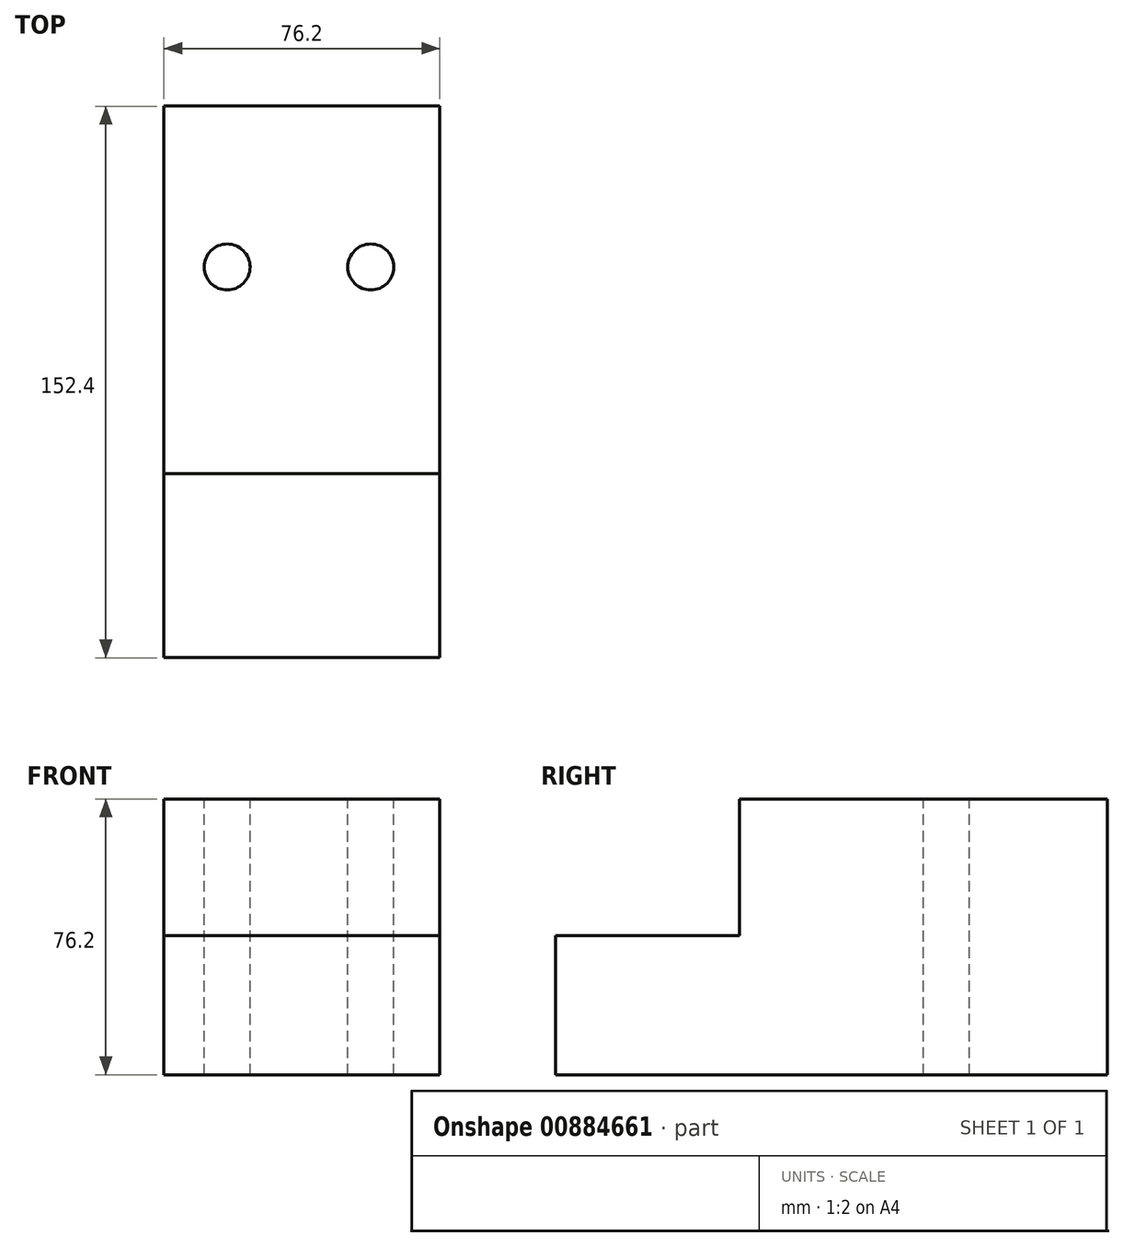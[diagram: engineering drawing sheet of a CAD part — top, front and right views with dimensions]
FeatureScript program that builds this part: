
annotation { "Feature Type Name" : "Feature", "Feature Type Description" : "" }
export const myFeature = defineFeature(function(context is Context, id is Id, definition is map)
    precondition{}
    {
        {
            var Q0;
            Q0=qCreatedBy(makeId("Top.planeOp"),FACE);
            var sketch = newSketch(context, id + "F0", { "sketchPlane" : qUnion([Q0])});
            skLineSegment(sketch, "E0.bottom", {"start": v(-21.8, 58.73) * mm, "end": v(54.4, 58.73) * mm});
            skLineSegment(sketch, "E0.top", {"start": v(-21.8, -93.67) * mm, "end": v(54.4, -93.67) * mm});
            skLineSegment(sketch, "E0.left", {"start": v(-21.8, 58.73) * mm, "end": v(-21.8, -93.67) * mm});
            skLineSegment(sketch, "E0.right", {"start": v(54.4, 58.73) * mm, "end": v(54.4, -93.67) * mm});
            skSolve(sketch);
        }
        {
            var Q0;
            Q0 = qSketchRegion(id + "F0", true);
            extrude(context, id + "F1", {"entities" : qUnion([Q0]), "depth" : 76.2 * mm, "offsetDistance" : 25.4 * mm});
        }
        {
            var Q0;
            Q0=makeQuery(id+"F1.opExtrude","CAP_FACE",FACE,{"disambiguationData":[OSD([sQuery(id+"F0.wireOp",EDGE,"E0.bottom"),sQuery(id+"F0.wireOp",EDGE,"E0.top"),sQuery(id+"F0.wireOp",EDGE,"E0.left"),sQuery(id+"F0.wireOp",EDGE,"E0.right")])],"isStart":false});
            var sketch = newSketch(context, id + "F2", { "sketchPlane" : qUnion([Q0])});
            skCircle(sketch, "E1", {"center": v(-4.36, 14.28) * mm, "radius": 6.35 * mm});
            skCircle(sketch, "E2", {"center": v(35.34, 14.28) * mm, "radius": 6.35 * mm});
            skSolve(sketch);
        }
        {
            var Q0;
            Q0=makeQuery(id+"F2.imprint","IMPRINT",FACE,{"disambiguationData":[TD([[makeQuery(id+"F2.imprint","IMPRINT",EDGE,{"derivedFrom":sQuery(id+"F2.wireOp",EDGE,"E1")}),1.0]])]});
            var Q1;
            Q1=makeQuery(id+"F2.imprint","IMPRINT",FACE,{"disambiguationData":[TD([[makeQuery(id+"F2.imprint","IMPRINT",EDGE,{"derivedFrom":sQuery(id+"F2.wireOp",EDGE,"E2")}),1.0]])]});
            extrude(context, id + "F3", {"entities" : qUnion([Q0, Q1]), "operationType" : NewBodyOperationType.REMOVE, "oppositeDirection" : true, "depth" : 76.2 * mm, "offsetDistance" : 25.4 * mm});
        }
        {
            var Q0;
            Q0=makeQuery(id+"F1.opExtrude","SWEPT_FACE",FACE,{"disambiguationData":[OSD([sQuery(id+"F0.wireOp",EDGE,"E0.top")])]});
            var sketch = newSketch(context, id + "F4", { "sketchPlane" : qUnion([Q0])});
            skLineSegment(sketch, "E3.bottom", {"start": v(-21.8, 76.5) * mm, "end": v(54.4, 76.5) * mm});
            skLineSegment(sketch, "E3.top", {"start": v(-21.8, 38.4) * mm, "end": v(54.4, 38.4) * mm});
            skLineSegment(sketch, "E3.left", {"start": v(-21.8, 76.5) * mm, "end": v(-21.8, 38.4) * mm});
            skLineSegment(sketch, "E3.right", {"start": v(54.4, 76.5) * mm, "end": v(54.4, 38.4) * mm});
            skSolve(sketch);
        }
        {
            var Q0;
            Q0 = qSketchRegion(id + "F4", true);
            extrude(context, id + "F5", {"entities" : qUnion([Q0]), "operationType" : NewBodyOperationType.REMOVE, "oppositeDirection" : true, "depth" : 25.4 * mm, "offsetDistance" : 25.4 * mm});
        }
        {
            var Q0;
            Q0 = qSketchRegion(id + "F4", true);
            extrude(context, id + "F6", {"entities" : qUnion([Q0]), "operationType" : NewBodyOperationType.REMOVE, "oppositeDirection" : true, "depth" : 50.8 * mm, "offsetDistance" : 25.4 * mm});
        }
    });
